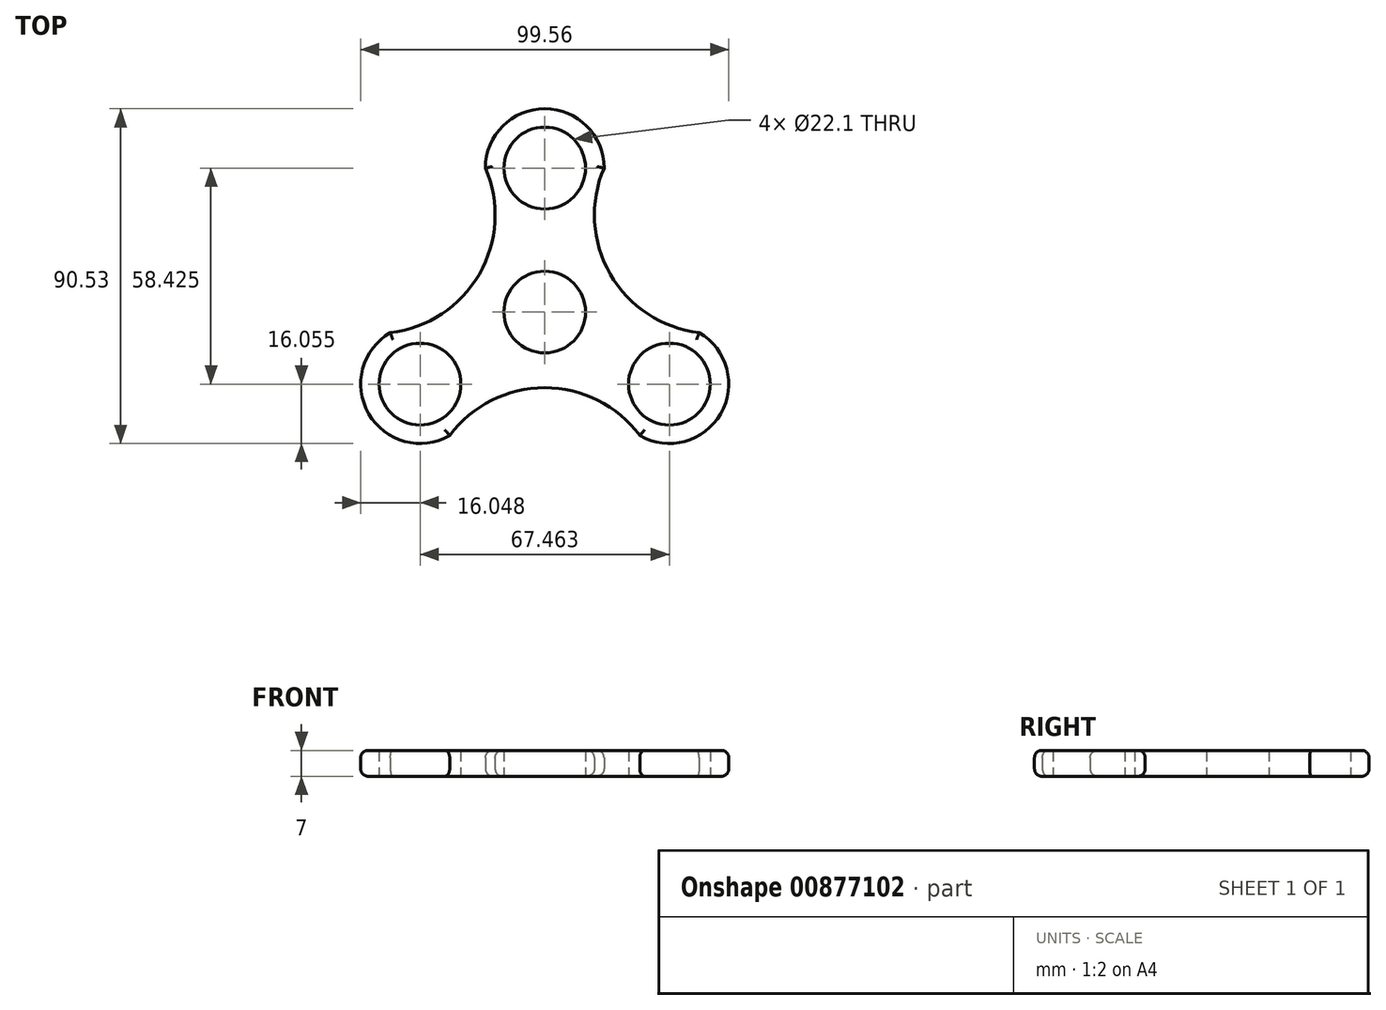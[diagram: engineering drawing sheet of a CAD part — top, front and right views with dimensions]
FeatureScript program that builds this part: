
annotation { "Feature Type Name" : "Feature", "Feature Type Description" : "" }
export const myFeature = defineFeature(function(context is Context, id is Id, definition is map)
    precondition{}
    {
        {
            var Q0;
            Q0=qCreatedBy(makeId("Top.planeOp"),FACE);
            var sketch = newSketch(context, id + "F0", { "sketchPlane" : qUnion([Q0])});
            skCircle(sketch, "E0", {"center": v(0, 0) * mm, "radius": 11.05 * mm});
            skCircle(sketch, "E1", {"center": v(0, 38.95) * mm, "radius": 11.05 * mm});
            skCircle(sketch, "E2.1.0", {"center": v(-33.73, -19.47) * mm, "radius": 11.05 * mm});
            skCircle(sketch, "E2.2.0", {"center": v(33.73, -19.48) * mm, "radius": 11.05 * mm});
            skArc(sketch, "E3", {"start": v(16.05, 38.95) * mm, "mid": v(0, 55) * mm, "end": v(-16.05, 38.95) * mm});
            skArc(sketch, "E4.1.0", {"start": v(-41.76, -5.58) * mm, "mid": v(-47.63, -27.5) * mm, "end": v(-25.7, -33.37) * mm});
            skArc(sketch, "E4.2.0", {"start": v(25.7, -33.37) * mm, "mid": v(47.63, -27.5) * mm, "end": v(41.76, -5.58) * mm});
            skArc(sketch, "E5", {"start": v(-41.76, -5.58) * mm, "mid": v(-17.72, 10.23) * mm, "end": v(-16.05, 38.95) * mm});
            skArc(sketch, "E6.1.0", {"start": v(25.7, -33.37) * mm, "mid": v(0, -20.46) * mm, "end": v(-25.7, -33.37) * mm});
            skArc(sketch, "E6.2.0", {"start": v(16.05, 38.95) * mm, "mid": v(17.72, 10.23) * mm, "end": v(41.76, -5.58) * mm});
            skSolve(sketch);
        }
        {
            var Q0;
            Q0=makeQuery(id+"F0.imprint","IMPRINT",FACE,{"disambiguationData":[TD([[makeQuery(id+"F0.imprint","IMPRINT",EDGE,{"derivedFrom":sQuery(id+"F0.wireOp",EDGE,"E0")}),-1.0]])]});
            extrude(context, id + "F1", {"entities" : qUnion([Q0]), "depth" : 7 * mm, "offsetDistance" : 25 * mm});
        }
        {
            var Q0;
            Q0=makeQuery(id+"F1.opExtrude","CAP_EDGE",EDGE,{"disambiguationData":[OSD([sQuery(id+"F0.wireOp",EDGE,"Pe4rpWo2-QfTQ-nDak-P9ll-lZfKN2u7p5Iy")])],"isStart":false});
            var Q1;
            Q1=makeQuery(id+"F1.opExtrude","CAP_EDGE",EDGE,{"disambiguationData":[OSD([sQuery(id+"F0.wireOp",EDGE,"E3")])],"isStart":false});
            var Q2;
            Q2=makeQuery(id+"F1.opExtrude","CAP_EDGE",EDGE,{"disambiguationData":[OSD([sQuery(id+"F0.wireOp",EDGE,"1ae6c461-0a8c-403e-ae2b-4c5a8630933d.2.0")])],"isStart":false});
            var Q3;
            Q3=makeQuery(id+"F1.opExtrude","CAP_EDGE",EDGE,{"disambiguationData":[OSD([sQuery(id+"F0.wireOp",EDGE,"E4.2.0")])],"isStart":false});
            var Q4;
            Q4=makeQuery(id+"F1.opExtrude","CAP_EDGE",EDGE,{"disambiguationData":[OSD([sQuery(id+"F0.wireOp",EDGE,"1ae6c461-0a8c-403e-ae2b-4c5a8630933d.1.0")])],"isStart":false});
            var Q5;
            Q5=makeQuery(id+"F1.opExtrude","CAP_EDGE",EDGE,{"disambiguationData":[OSD([sQuery(id+"F0.wireOp",EDGE,"E4.1.0")])],"isStart":false});
            var Q6;
            Q6=makeQuery(id+"F1.opExtrude","CAP_EDGE",EDGE,{"disambiguationData":[OSD([sQuery(id+"F0.wireOp",EDGE,"E4.1.0")])],"isStart":true});
            var Q7;
            Q7=makeQuery(id+"F1.opExtrude","CAP_EDGE",EDGE,{"disambiguationData":[OSD([sQuery(id+"F0.wireOp",EDGE,"Pe4rpWo2-QfTQ-nDak-P9ll-lZfKN2u7p5Iy")])],"isStart":true});
            var Q8;
            Q8=makeQuery(id+"F1.opExtrude","CAP_EDGE",EDGE,{"disambiguationData":[OSD([sQuery(id+"F0.wireOp",EDGE,"E3")])],"isStart":true});
            var Q9;
            Q9=makeQuery(id+"F1.opExtrude","CAP_EDGE",EDGE,{"disambiguationData":[OSD([sQuery(id+"F0.wireOp",EDGE,"1ae6c461-0a8c-403e-ae2b-4c5a8630933d.2.0")])],"isStart":true});
            var Q10;
            Q10=makeQuery(id+"F1.opExtrude","CAP_EDGE",EDGE,{"disambiguationData":[OSD([sQuery(id+"F0.wireOp",EDGE,"E4.2.0")])],"isStart":true});
            var Q11;
            Q11=makeQuery(id+"F1.opExtrude","CAP_EDGE",EDGE,{"disambiguationData":[OSD([sQuery(id+"F0.wireOp",EDGE,"1ae6c461-0a8c-403e-ae2b-4c5a8630933d.1.0")])],"isStart":true});
            var Q12;
            Q12=makeQuery(id+"F1.opExtrude","CAP_EDGE",EDGE,{"disambiguationData":[OSD([sQuery(id+"F0.wireOp",EDGE,"E5")])],"isStart":true});
            var Q13;
            Q13=makeQuery(id+"F1.opExtrude","CAP_EDGE",EDGE,{"disambiguationData":[OSD([sQuery(id+"F0.wireOp",EDGE,"E5")])],"isStart":false});
            var Q14;
            Q14=makeQuery(id+"F1.opExtrude","CAP_EDGE",EDGE,{"disambiguationData":[OSD([sQuery(id+"F0.wireOp",EDGE,"E6.2.0")])],"isStart":true});
            var Q15;
            Q15=makeQuery(id+"F1.opExtrude","CAP_EDGE",EDGE,{"disambiguationData":[OSD([sQuery(id+"F0.wireOp",EDGE,"E6.2.0")])],"isStart":false});
            var Q16;
            Q16=makeQuery(id+"F1.opExtrude","CAP_EDGE",EDGE,{"disambiguationData":[OSD([sQuery(id+"F0.wireOp",EDGE,"E6.1.0")])],"isStart":false});
            var Q17;
            Q17=makeQuery(id+"F1.opExtrude","CAP_EDGE",EDGE,{"disambiguationData":[OSD([sQuery(id+"F0.wireOp",EDGE,"E6.1.0")])],"isStart":true});
            fillet(context, id + "F2", {"entities" : qUnion([Q0, Q1, Q2, Q3, Q4, Q5, Q6, Q7, Q8, Q9, Q10, Q11, Q12, Q13, Q14, Q15, Q16, Q17]), "radius" : 2 * mm, "tangentPropagation" : true, "allowEdgeOverflow" : false});
        }
    });
